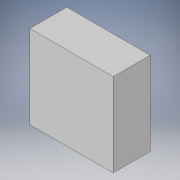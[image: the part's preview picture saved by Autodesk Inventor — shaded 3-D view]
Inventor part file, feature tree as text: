
AUTODESK INVENTOR PART (.ipt)
format: ipt  version: 2018 (Build 220112000, 112)  size: 86,016 bytes
history: native  units: in
note: dims shown in document units (in); Inventor stores cm internally (conversion verified against a paired STEP export)
features: extrude x1, sketch x1
ambient origin geometry x8: Origin, YZ Plane, XZ Plane, XY Plane, X Axis, Y Axis, Z Axis, Center Point
bodies: Solid1 (feature_tree)
feature tree (2):
  extrude  "Extrusion1"  Depth=0.6201in
  sketch  "Sketch1"  dims[d0=0.6201in d1=0.6201in d2=0.2756in d3=0.0in]
